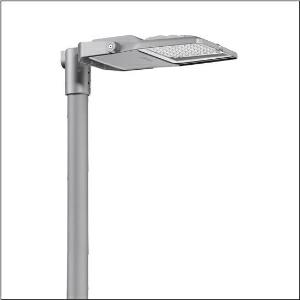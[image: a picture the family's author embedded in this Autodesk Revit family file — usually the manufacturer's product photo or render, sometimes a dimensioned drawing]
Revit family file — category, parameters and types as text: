
# Revit family: floodlight_fl_21_mini___pl43_5xa7775d2a3a_0001
name_source: partatom
category: Lighting Fixtures
units: mm (PartAtom-declared; Revit-internal decimal feet)

## family parameters
Cut with Voids When Loaded = No
Host = Face
Light Source = No
Part Type = Normal
Room Calculation Point = No
Round Connector Dimension = Use Diameter
Shared = No

## types (1)
- --- (1 x LED, 18300 lm, 142.9 W, 3000K)
    Apparent Load = 143 VA
    CIE Flux Codes = 27 78 99 100 100
    Color Rendering = 70
    Color Temperature = 3000K
    Default Elevation = 1800 mm
    Description = Floodlight FL 21 mini, floodlight, primary light control with lens, of PMMA, primary optical cover: protective disc, of toughened safety glass, transparent, light distribution: PL43, light emission: direct distribution, installation type: surface-mounted, LED, High Power LED, rated luminous flux: 18.300lm, luminous efficacy: 128lm/W, light colour: 730, colour temperature: 3000K, control: flexible luminous flux parameterisation, time-dependent luminous flux control, constant luminous flux control, overheat protection, presetting dimming logarithmic, with terminal, 6-pole, mains connection: 220..240V, AC, 50/60Hz, start of lifetime: 143W, end of service life: 151W, reduction: 63W, luminaire housing, of diecast aluminium, powder-coated, Siteco® metallic grey (DB 702S), corrosivity category C5 mid according to DIN EN ISO 12944, sealing non-destructively replaceable, please order mast flange separately, mast bracket, of steel, galvanised, powder-coated, Siteco® metallic grey (DB 702S), Smart Interface above, protection rating (complete): IP66, insulation class (complete): insulation class II (safety insulation), certification: CE, ENEC, VDE, protection symbol: D, impact resistance: IK08, permissible operating ambient temperature: -40..+40°C, permissible operating ambient temperature for outdoor applications: -40..+50°C, standard: DIN EN 12944, LABS conformity tested according to VDMA 24364:2018-05, packaging unit: 1 piece

Light Distribution: PL43
    Height = 70 mm
    Lamp = 1 x LED
    Lamp Light Flux = 18300 lm
    Lamp Power = 142.9 W
    Lamp count = 1
    Length = 485 mm
    Luminous efficacy = 128 lm/W
    Manufacturer = Siteco
    ModVariant = No
    Model = 5XA7775D2A3A
    Number of Poles = 1
    OnlyDefault = Yes
    Power Factor = 1
    Product Name = Floodlight FL 21 mini | PL43
    Product group = floodlight | pylon annexe
    ProductGroupID = 6200
    Protection Class = Protection class II
    Protection Degree = IP 66
    RLX_Detail_Level = 1
    RLX_Emergency_Light_Flux = 0 lm
    RLX_Emergency_Type = 0
    RLX_Emergency_Type_DB = No
    RlxData = <blob elided: 101153 chars, md5=4a139bd6>
    Socket = socket
    Standby Power = 0 W
    System Light Flux = 18300 lm
    System Power = 143 W
    Type Comments = factory setting: luminous flux: 100 % | dim-lin: 254 | 730 mA
    Type Image = l_1007125.jpg
    URL = http://relux.com
    VarID = @adj_111139
    Voltage = 0 V
    Weight = 0.00 kg
    Width = 337 mm

## geometry (parser evidence)
native form markers: Blend x4, Sweep x13
no freeform markers — native parametric forms only
